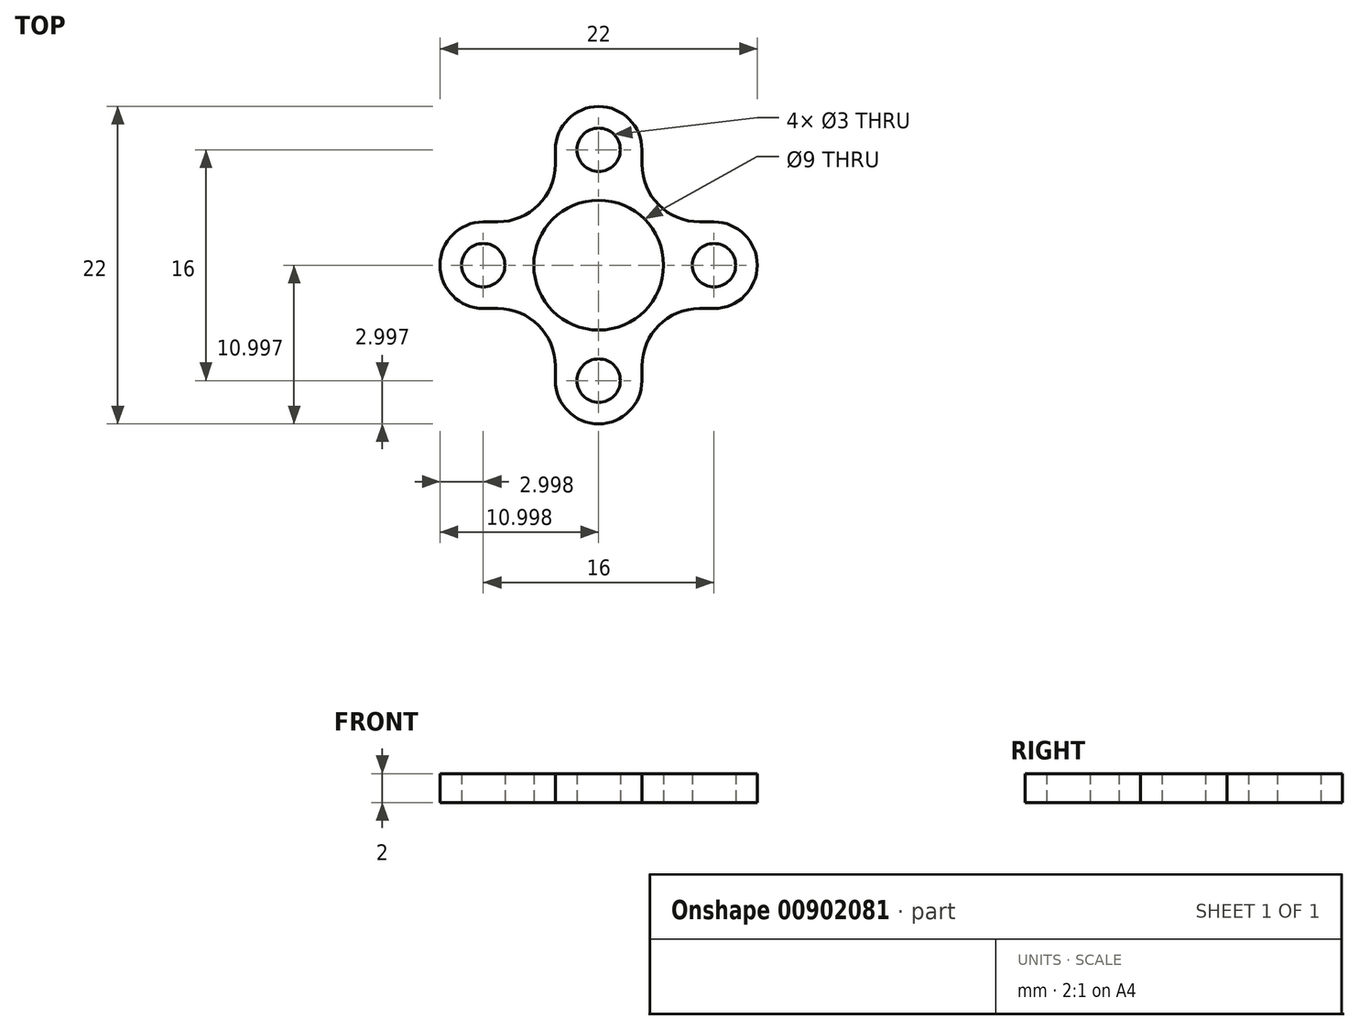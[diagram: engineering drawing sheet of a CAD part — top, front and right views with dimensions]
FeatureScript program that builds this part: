
annotation { "Feature Type Name" : "Feature", "Feature Type Description" : "" }
export const myFeature = defineFeature(function(context is Context, id is Id, definition is map)
    precondition{}
    {
        {
            var Q0;
            Q0=qCreatedBy(makeId("Top.planeOp"),FACE);
            var sketch = newSketch(context, id + "F0", { "sketchPlane" : qUnion([Q0])});
            skCircle(sketch, "E0", {"center": v(-0.33, -0.01) * mm, "radius": 8 * mm, "construction": true});
            skCircle(sketch, "E1", {"center": v(-0.33, 7.99) * mm, "radius": 1.5 * mm});
            skCircle(sketch, "E2", {"center": v(-8.33, -0.01) * mm, "radius": 1.5 * mm});
            skCircle(sketch, "E3", {"center": v(7.67, -0.01) * mm, "radius": 1.5 * mm});
            skCircle(sketch, "E4", {"center": v(-0.33, -8.01) * mm, "radius": 1.5 * mm});
            skCircle(sketch, "E5", {"center": v(-0.33, -0.01) * mm, "radius": 5.5 * mm, "construction": true});
            skLineSegment(sketch, "E6", {"start": v(-13.05, 12.7) * mm, "end": v(-0.33, -0.01) * mm, "construction": true});
            skLineSegment(sketch, "E7", {"start": v(-0.33, -0.01) * mm, "end": v(13.46, -13.8) * mm, "construction": true});
            skLineSegment(sketch, "E8", {"start": v(12.42, 12.74) * mm, "end": v(-0.33, -0.01) * mm, "construction": true});
            skLineSegment(sketch, "E9", {"start": v(-0.33, -0.01) * mm, "end": v(-11.08, -10.76) * mm, "construction": true});
            skLineSegment(sketch, "E10", {"start": v(-0.33, -0.01) * mm, "end": v(19.86, -0.01) * mm, "construction": true});
            skCircle(sketch, "E11", {"center": v(-0.33, 7.99) * mm, "radius": 3 * mm, "construction": true});
            skCircle(sketch, "E12", {"center": v(-8.33, -0.01) * mm, "radius": 3 * mm, "construction": true});
            skCircle(sketch, "E13", {"center": v(-0.33, -8.01) * mm, "radius": 3 * mm, "construction": true});
            skCircle(sketch, "E14", {"center": v(7.67, -0.01) * mm, "radius": 3 * mm, "construction": true});
            skLineSegment(sketch, "E15", {"start": v(-8.33, -3.01) * mm, "end": v(-7.33, -3.01) * mm});
            skLineSegment(sketch, "E16", {"start": v(-3.33, -7.01) * mm, "end": v(-3.33, -8.01) * mm});
            skLineSegment(sketch, "E17", {"start": v(2.67, -8.01) * mm, "end": v(2.67, -7.01) * mm});
            skLineSegment(sketch, "E18", {"start": v(6.67, -3.01) * mm, "end": v(7.67, -3.01) * mm});
            skLineSegment(sketch, "E19", {"start": v(7.67, 2.99) * mm, "end": v(6.67, 2.99) * mm});
            skLineSegment(sketch, "E20", {"start": v(2.67, 6.99) * mm, "end": v(2.67, 7.99) * mm});
            skLineSegment(sketch, "E21", {"start": v(-3.33, 7.99) * mm, "end": v(-3.33, 6.99) * mm});
            skLineSegment(sketch, "E22", {"start": v(-7.33, 2.99) * mm, "end": v(-8.33, 2.99) * mm});
            skArc(sketch, "E23", {"start": v(-8.33, -3.01) * mm, "mid": v(-11.33, -0.01) * mm, "end": v(-8.33, 2.99) * mm});
            skArc(sketch, "E24", {"start": v(-3.33, 7.99) * mm, "mid": v(-0.33, 10.99) * mm, "end": v(2.67, 7.99) * mm});
            skArc(sketch, "E25", {"start": v(7.67, 2.99) * mm, "mid": v(10.67, -0.01) * mm, "end": v(7.67, -3.01) * mm});
            skArc(sketch, "E26", {"start": v(2.67, -8.01) * mm, "mid": v(-0.33, -11.01) * mm, "end": v(-3.33, -8.01) * mm});
            skPoint(sketch, "E27.visualSharp", {"position": v(-3.33, 2.99) * mm});
            skArc(sketch, "E27.filletArc", {"start": v(-7.33, 2.99) * mm, "mid": v(-4.5, 4.16) * mm, "end": v(-3.33, 6.99) * mm});
            skPoint(sketch, "E28.visualSharp", {"position": v(2.67, 2.99) * mm});
            skArc(sketch, "E28.filletArc", {"start": v(2.67, 6.99) * mm, "mid": v(3.84, 4.16) * mm, "end": v(6.67, 2.99) * mm});
            skPoint(sketch, "E29.visualSharp", {"position": v(2.67, -3.01) * mm});
            skArc(sketch, "E29.filletArc", {"start": v(6.67, -3.01) * mm, "mid": v(3.84, -4.18) * mm, "end": v(2.67, -7.01) * mm});
            skPoint(sketch, "E30.visualSharp", {"position": v(-3.33, -3.01) * mm});
            skArc(sketch, "E30.filletArc", {"start": v(-3.33, -7.01) * mm, "mid": v(-4.5, -4.18) * mm, "end": v(-7.33, -3.01) * mm});
            skCircle(sketch, "E31", {"center": v(-0.33, -0.01) * mm, "radius": 4.5 * mm});
            skSolve(sketch);
        }
        {
            var Q0;
            Q0 = qSketchRegion(id + "F0", true);
            extrude(context, id + "F1", {"entities" : qUnion([Q0]), "depth" : 2 * mm, "offsetDistance" : 25.4 * mm});
        }
    });
